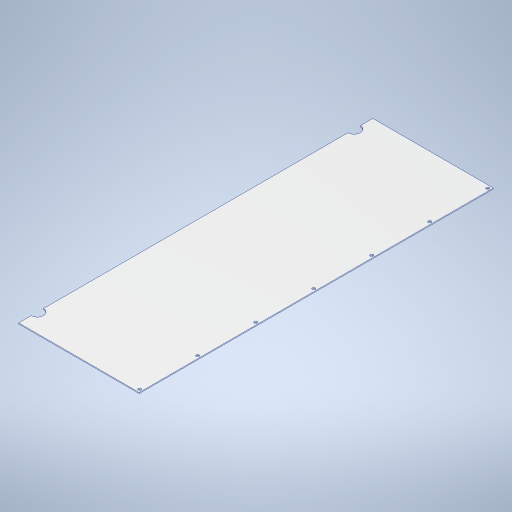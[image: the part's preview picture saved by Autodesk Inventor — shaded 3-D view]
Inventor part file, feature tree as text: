
AUTODESK INVENTOR PART (.ipt)
format: ipt  version: 2023 (Build 270158000, 158)  size: 263,680 bytes
history: native  units: in
note: dims shown in document units (in); Inventor stores cm internally (conversion verified against a paired STEP export)
features: sketch x3, hole x2, sheet_metal_op x1, pattern_linear x1, other x1
ambient origin geometry x8: Origin, YZ Plane, XZ Plane, XY Plane, X Axis, Y Axis, Z Axis, Center Point
bodies: Solid1 (feature_tree)
feature tree (8):
  sheet_metal_op  "Face1"
  hole  "Hole1"  [1 undecoded]
  pattern_linear  "Rectangular Pattern1"  Spacing1=0.0625in  [1 undecoded]
  hole  "Hole2"  [1 undecoded]
  sketch  "Sketch1"  dims[d0=7.6378in d1=22.4409in]
  other  "Plate1"
  sketch  "Sketch4"  dims[d2=3.8189in]
  sketch  "Sketch5"  dims[d3=11.2205in d4=0.0625in d15=0.194in d16=0.2953in d17=0.1476in d18=0.0984in d19=90.0deg d20=0.0625in d21=0.8108in d22=0.1939in d23=2.7559in d25=3.6755in d28=0.7874in d29=0.2953in d30=0.1476in d31=0.0984in d32=90.0deg d33=0.3937in d34=0.8108in d35=1.1811in d36=1.1811in d40=0.162in]
note: 3 required parameter values undecoded (feature->parameter linkage not recoverable at this tier; creation-order binding heuristic only, values carry confidence <= 0.55)
